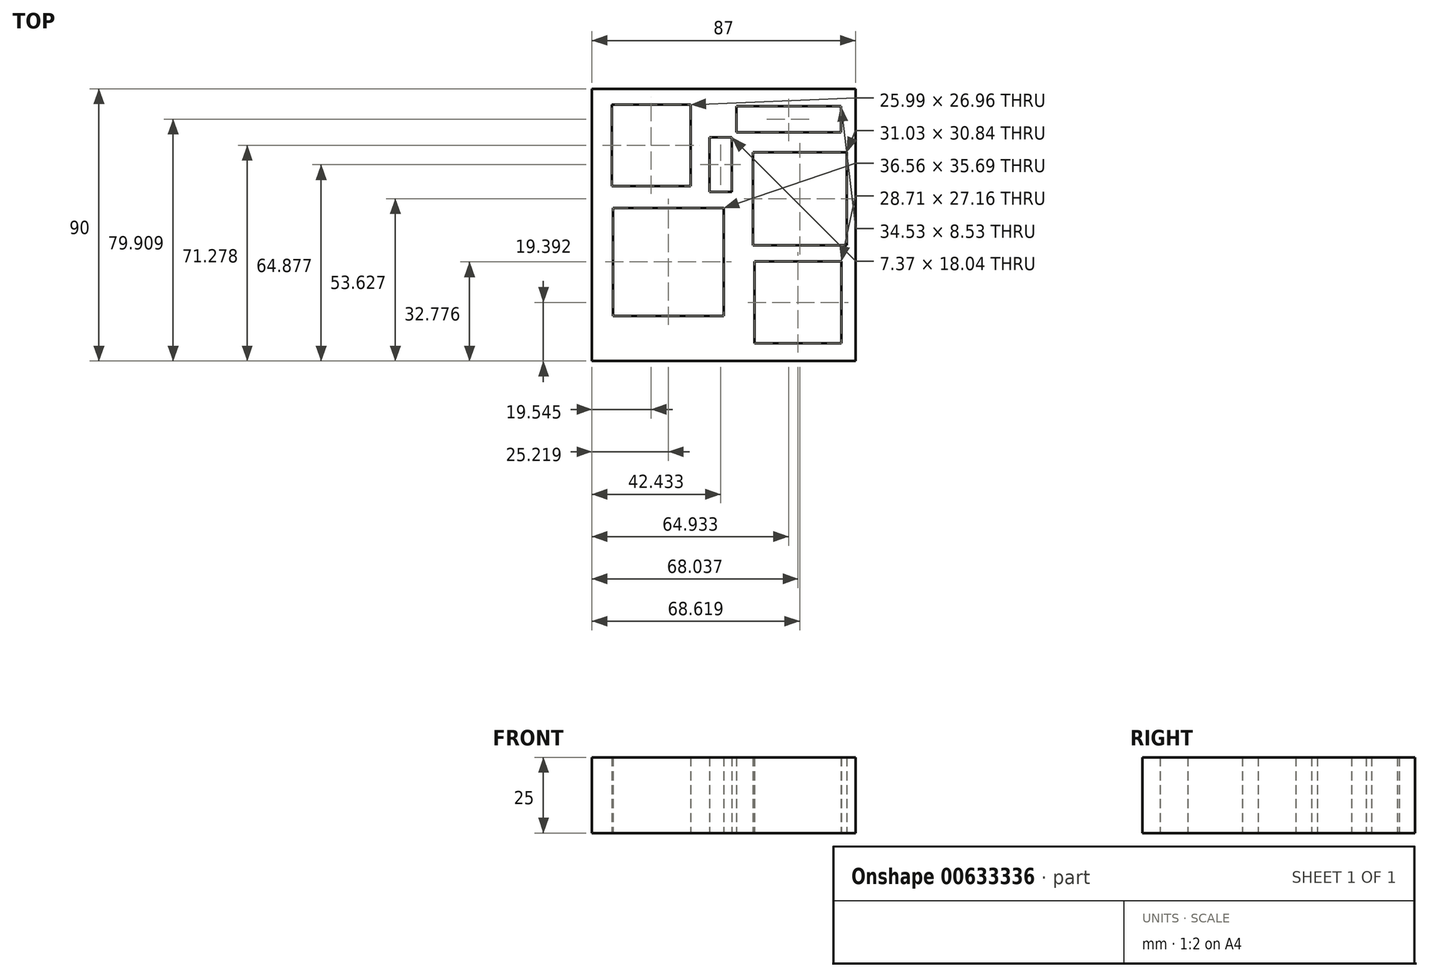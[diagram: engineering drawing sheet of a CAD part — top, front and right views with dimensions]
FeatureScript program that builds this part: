
annotation { "Feature Type Name" : "Feature", "Feature Type Description" : "" }
export const myFeature = defineFeature(function(context is Context, id is Id, definition is map)
    precondition{}
    {
        {
            var Q0;
            Q0=qCreatedBy(makeId("Top.planeOp"),FACE);
            var sketch = newSketch(context, id + "F0", { "sketchPlane" : qUnion([Q0])});
            skLineSegment(sketch, "E0.bottom", {"start": v(43.5, 43.55) * mm, "end": v(-43.5, 43.55) * mm});
            skLineSegment(sketch, "E0.top", {"start": v(43.5, -46.45) * mm, "end": v(-43.5, -46.45) * mm});
            skLineSegment(sketch, "E0.left", {"start": v(43.5, 43.55) * mm, "end": v(43.5, -46.45) * mm});
            skLineSegment(sketch, "E0.right", {"start": v(-43.5, 43.55) * mm, "end": v(-43.5, -46.45) * mm});
            skPoint(sketch, "E0.middle", {"position": v(0, -1.45) * mm});
            skLineSegment(sketch, "E1.bottom", {"start": v(-36.95, 38.3) * mm, "end": v(-10.96, 38.3) * mm});
            skLineSegment(sketch, "E1.top", {"start": v(-36.95, 11.35) * mm, "end": v(-10.96, 11.35) * mm});
            skLineSegment(sketch, "E1.left", {"start": v(-36.95, 38.3) * mm, "end": v(-36.95, 11.35) * mm});
            skLineSegment(sketch, "E1.right", {"start": v(-10.96, 38.3) * mm, "end": v(-10.96, 11.35) * mm});
            skLineSegment(sketch, "E2.bottom", {"start": v(9.6, 22.6) * mm, "end": v(40.64, 22.6) * mm});
            skLineSegment(sketch, "E2.top", {"start": v(9.6, -8.24) * mm, "end": v(40.64, -8.24) * mm});
            skLineSegment(sketch, "E2.left", {"start": v(9.6, 22.6) * mm, "end": v(9.6, -8.24) * mm});
            skLineSegment(sketch, "E2.right", {"start": v(40.64, 22.6) * mm, "end": v(40.64, -8.24) * mm});
            skLineSegment(sketch, "E3.bottom", {"start": v(-36.56, 4.17) * mm, "end": v(0, 4.17) * mm});
            skLineSegment(sketch, "E3.top", {"start": v(-36.56, -31.52) * mm, "end": v(0, -31.52) * mm});
            skLineSegment(sketch, "E3.left", {"start": v(-36.56, 4.17) * mm, "end": v(-36.56, -31.52) * mm});
            skLineSegment(sketch, "E3.right", {"start": v(0, 4.17) * mm, "end": v(0, -31.52) * mm});
            skLineSegment(sketch, "E4.bottom", {"start": v(10.18, -13.48) * mm, "end": v(38.9, -13.48) * mm});
            skLineSegment(sketch, "E4.top", {"start": v(10.18, -40.64) * mm, "end": v(38.9, -40.64) * mm});
            skLineSegment(sketch, "E4.left", {"start": v(10.18, -13.48) * mm, "end": v(10.18, -40.64) * mm});
            skLineSegment(sketch, "E4.right", {"start": v(38.9, -13.48) * mm, "end": v(38.9, -40.64) * mm});
            skLineSegment(sketch, "E5.bottom", {"start": v(4.17, 37.73) * mm, "end": v(38.7, 37.73) * mm});
            skLineSegment(sketch, "E5.top", {"start": v(4.17, 29.2) * mm, "end": v(38.7, 29.2) * mm});
            skLineSegment(sketch, "E5.left", {"start": v(4.17, 37.73) * mm, "end": v(4.17, 29.2) * mm});
            skLineSegment(sketch, "E5.right", {"start": v(38.7, 37.73) * mm, "end": v(38.7, 29.2) * mm});
            skLineSegment(sketch, "E6.bottom", {"start": v(-4.75, 27.45) * mm, "end": v(2.62, 27.45) * mm});
            skLineSegment(sketch, "E6.top", {"start": v(-4.75, 9.4) * mm, "end": v(2.62, 9.4) * mm});
            skLineSegment(sketch, "E6.left", {"start": v(-4.75, 27.45) * mm, "end": v(-4.75, 9.4) * mm});
            skLineSegment(sketch, "E6.right", {"start": v(2.62, 27.45) * mm, "end": v(2.62, 9.4) * mm});
            skSolve(sketch);
        }
        {
            var Q0;
            Q0=makeQuery(id+"F0.imprint","IMPRINT",FACE,{"disambiguationData":[TD([[makeQuery(id+"F0.imprint","IMPRINT",EDGE,{"derivedFrom":sQuery(id+"F0.wireOp",EDGE,"E0.bottom")}),1.0]])]});
            extrude(context, id + "F1", {"entities" : qUnion([Q0]), "depth" : 25 * mm, "offsetDistance" : 25 * mm});
        }
    });
